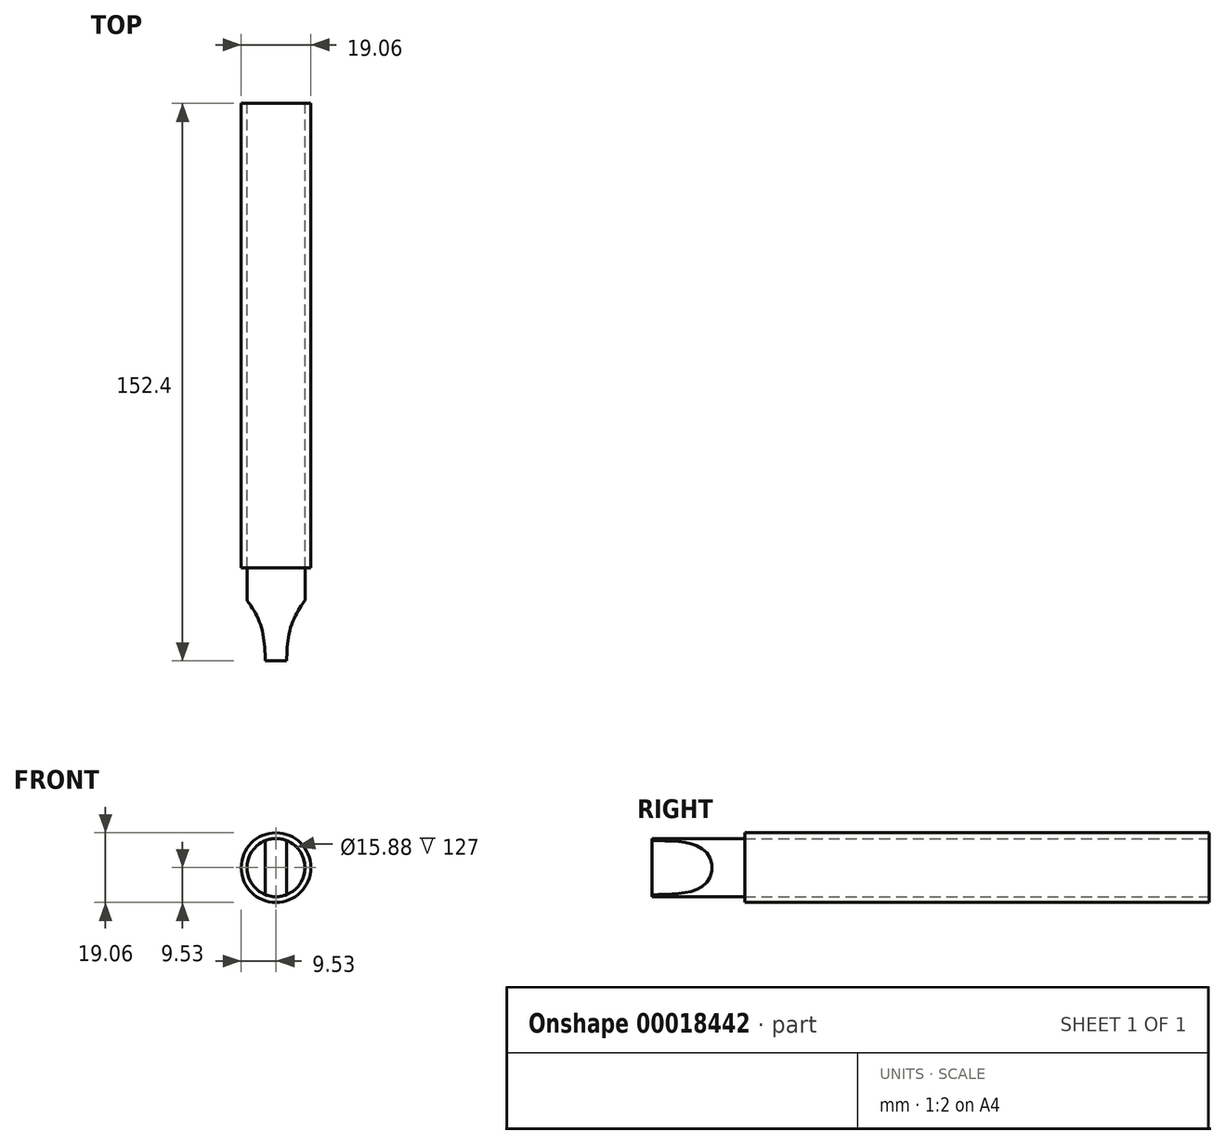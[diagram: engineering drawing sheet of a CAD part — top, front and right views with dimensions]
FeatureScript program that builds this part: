
annotation { "Feature Type Name" : "Feature", "Feature Type Description" : "" }
export const myFeature = defineFeature(function(context is Context, id is Id, definition is map)
    precondition{}
    {
        {
            var Q0;
            Q0=qCreatedBy(makeId("Front.planeOp"),FACE);
            var sketch = newSketch(context, id + "F0", { "sketchPlane" : qUnion([Q0])});
            skCircle(sketch, "E0", {"center": v(0, 0) * mm, "radius": 9.53 * mm});
            skSolve(sketch);
        }
        {
            var Q0;
            Q0=makeQuery(id+"F0.imprint","IMPRINT",FACE,{"disambiguationData":[TD([[makeQuery(id+"F0.imprint","IMPRINT",EDGE,{"derivedFrom":sQuery(id+"F0.wireOp",EDGE,"E0")}),1.0]])]});
            extrude(context, id + "F1", {"entities" : qUnion([Q0]), "depth" : 127 * mm});
        }
        {
            var Q0;
            Q0=qCreatedBy(makeId("Front.planeOp"),FACE);
            var sketch = newSketch(context, id + "F2", { "sketchPlane" : qUnion([Q0])});
            skPoint(sketch, "E1", {"position": v(0, 0) * mm});
            skSolve(sketch);
        }
        {
            var Q0;
            Q0=sQuery(id+"F2.wireOp",VERTEX,"E1");
            var Q1;
            Q1=makeQuery(id+"F1.opExtrude","SWEPT_BODY",BODY,{"disambiguationData":[OSD([sQuery(id+"F0.wireOp",EDGE,"E0")])]});
            hole(context, id + "F3", {"style" : HoleStyle.SIMPLE, "holeDiameter" : 15.88 * mm, "endStyle" : HoleEndStyle.THROUGH, "oppositeDirection" : true, "locations" : qUnion([Q0]), "scope" : qUnion([Q1])});
        }
        {
            var Q0;
            Q0=qCreatedBy(makeId("Front.planeOp"),FACE);
            cPlane(context, id + "F4", {"entities" : qUnion([Q0]), "cplaneType" : CPlaneType.OFFSET, "offset" : 127 * mm, "width" : 152.4 * mm, "height" : 152.4 * mm});
        }
        {
            var Q0;
            Q0=qCreatedBy(id+"F4.planeOp",FACE);
            var sketch = newSketch(context, id + "F5", { "sketchPlane" : qUnion([Q0])});
            skCircle(sketch, "E2.0", {"center": v(0, 0) * mm, "radius": 7.94 * mm});
            skSolve(sketch);
        }
        {
            var Q0;
            Q0=makeQuery(id+"F5.imprint","IMPRINT",FACE,{"disambiguationData":[TD([[makeQuery(id+"F5.imprint","IMPRINT",EDGE,{"derivedFrom":sQuery(id+"F5.wireOp",EDGE,"E2.0")}),1.0]])]});
            extrude(context, id + "F6", {"entities" : qUnion([Q0]), "depth" : 25.4 * mm});
        }
        {
            var Q0;
            Q0=qCreatedBy(makeId("Top.planeOp"),FACE);
            var sketch = newSketch(context, id + "F7", { "sketchPlane" : qUnion([Q0])});
            skLineSegment(sketch, "E3", {"start": v(0, -158.85) * mm, "end": v(0, -126.1) * mm});
            skFitSpline(sketch, "E4", {"points": [v(2.88, -152.82) * mm, v(4, -143.3) * mm, v(8.52, -135.15) * mm], "startDerivative": vector(0.45, 14.44) * mm, "endDerivative": vector(11.18, 13.97) * mm});
            skLineSegment(sketch, "E5", {"start": v(2.88, -152.82) * mm, "end": v(8.46, -152.82) * mm});
            skLineSegment(sketch, "E6", {"start": v(8.46, -152.82) * mm, "end": v(8.52, -135.15) * mm});
            skFitSpline(sketch, "E7.MirrorCS", {"points": [v(-2.88, -152.82) * mm, v(-4, -143.3) * mm, v(-8.52, -135.15) * mm], "startDerivative": vector(-0.45, 14.44) * mm, "endDerivative": vector(-11.18, 13.97) * mm});
            skLineSegment(sketch, "E8.MirrorCS", {"start": v(-8.46, -152.82) * mm, "end": v(-8.52, -135.15) * mm});
            skLineSegment(sketch, "E9.MirrorCS", {"start": v(-2.88, -152.82) * mm, "end": v(-8.46, -152.82) * mm});
            skSolve(sketch);
        }
        {
            var Q0;
            Q0=makeQuery(id+"F7.imprint","IMPRINT",FACE,{"disambiguationData":[TD([[makeQuery(id+"F7.imprint","IMPRINT",EDGE,{"derivedFrom":sQuery(id+"F7.wireOp",EDGE,"E4")}),-1.0]])]});
            var Q1;
            Q1=makeQuery(id+"F7.imprint","IMPRINT",FACE,{"disambiguationData":[TD([[makeQuery(id+"F7.imprint","IMPRINT",EDGE,{"derivedFrom":sQuery(id+"F7.wireOp",EDGE,"E7.MirrorCS")}),1.0]])]});
            extrude(context, id + "F8", {"entities" : qUnion([Q0, Q1]), "operationType" : NewBodyOperationType.REMOVE, "depth" : 25.4 * mm, "hasSecondDirection" : true, "secondDirectionOppositeDirection" : true, "secondDirectionDepth" : 25.4 * mm});
        }
    });
